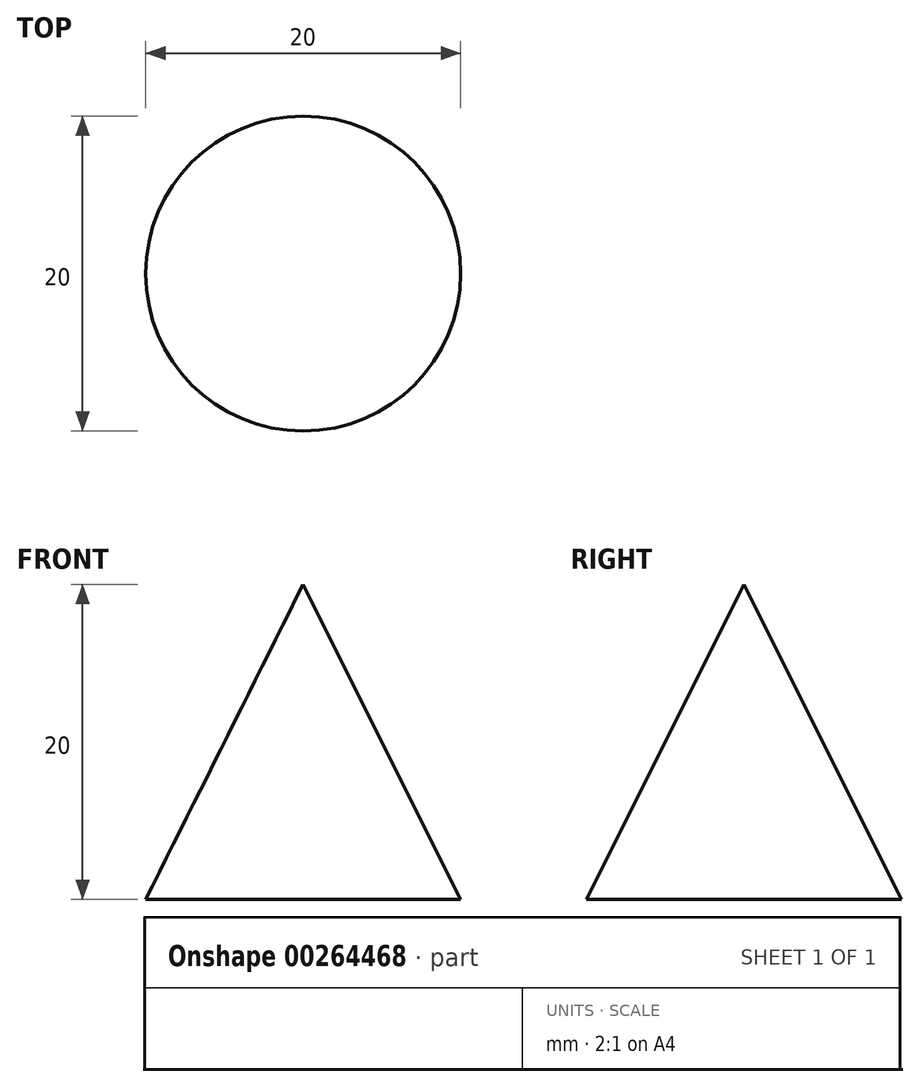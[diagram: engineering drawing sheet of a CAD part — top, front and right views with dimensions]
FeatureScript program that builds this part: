
annotation { "Feature Type Name" : "Feature", "Feature Type Description" : "" }
export const myFeature = defineFeature(function(context is Context, id is Id, definition is map)
    precondition{}
    {
        {
            var Q0;
            Q0=qCreatedBy(makeId("Front.planeOp"),FACE);
            var sketch = newSketch(context, id + "F0", { "sketchPlane" : qUnion([Q0])});
            skLineSegment(sketch, "E0", {"start": v(0, 0) * mm, "end": v(-10, 0) * mm});
            skLineSegment(sketch, "E1", {"start": v(-10, 0) * mm, "end": v(0, 20) * mm});
            skLineSegment(sketch, "E2", {"start": v(0, 20) * mm, "end": v(0, 0) * mm});
            skSolve(sketch);
        }
        {
            var Q0;
            Q0=makeQuery(id+"F0.imprint","IMPRINT",FACE,{"disambiguationData":[TD([[makeQuery(id+"F0.imprint","IMPRINT",EDGE,{"derivedFrom":sQuery(id+"F0.wireOp",EDGE,"E0")}),-1.0]])]});
            var Q1;
            Q1=sQuery(id+"F0.wireOp",EDGE,"E2");
            revolve(context, id + "F1", {"entities" : qUnion([Q0]), "axis" : qUnion([Q1]), "revolveType" : RevolveType.FULL});
        }
    });
